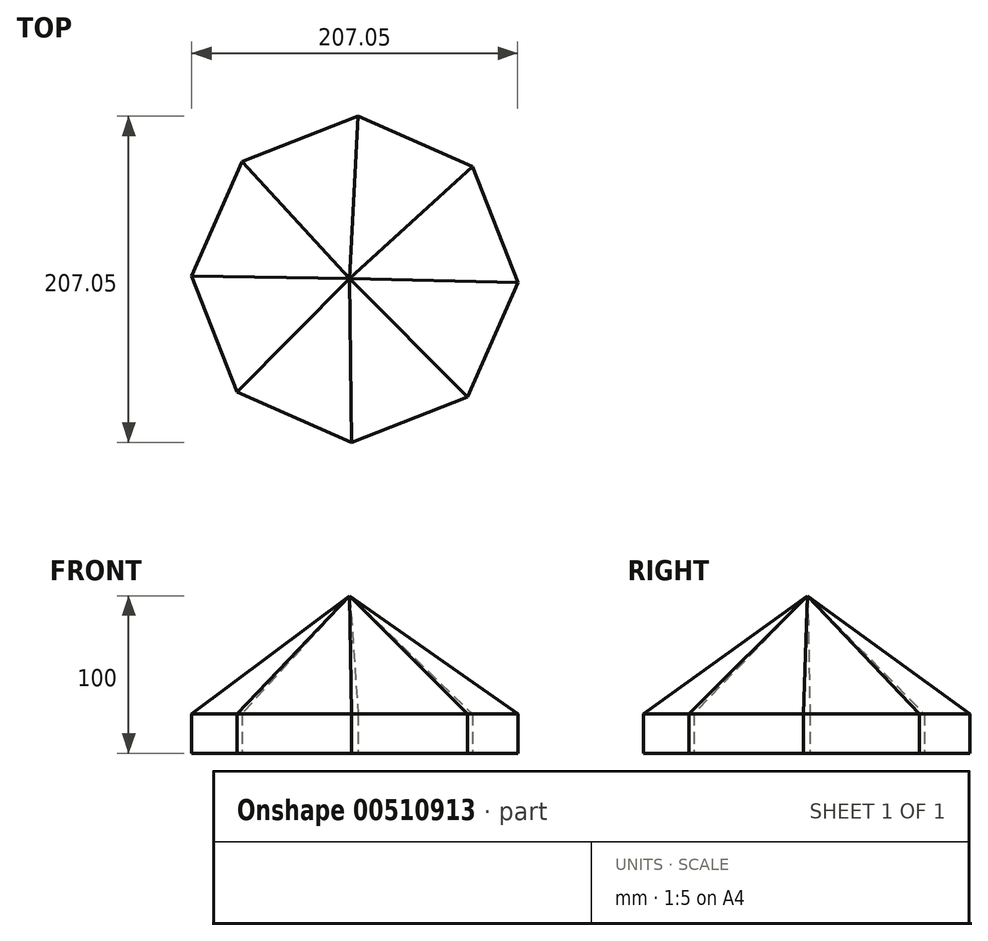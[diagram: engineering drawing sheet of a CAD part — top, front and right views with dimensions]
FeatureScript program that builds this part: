
annotation { "Feature Type Name" : "Feature", "Feature Type Description" : "" }
export const myFeature = defineFeature(function(context is Context, id is Id, definition is map)
    precondition{}
    {
        {
            var Q0;
            Q0=qCreatedBy(makeId("Top.planeOp"),FACE);
            var sketch = newSketch(context, id + "F0", { "sketchPlane" : qUnion([Q0])});
            skCircle(sketch, "E0.cCircle", {"center": v(-3.08, 12.36) * mm, "radius": 103.55 * mm, "construction": true});
            skLineSegment(sketch, "E0.0", {"start": v(-5.18, -91.16) * mm, "end": v(-77.77, -59.35) * mm});
            skLineSegment(sketch, "E0.1", {"start": v(-77.77, -59.35) * mm, "end": v(-106.6, 14.46) * mm});
            skLineSegment(sketch, "E0.2", {"start": v(-106.6, 14.46) * mm, "end": v(-74.8, 87.05) * mm});
            skLineSegment(sketch, "E0.3", {"start": v(-74.8, 87.05) * mm, "end": v(-0.98, 115.89) * mm});
            skLineSegment(sketch, "E0.4", {"start": v(-0.98, 115.89) * mm, "end": v(71.61, 84.08) * mm});
            skLineSegment(sketch, "E0.5", {"start": v(71.61, 84.08) * mm, "end": v(100.44, 10.26) * mm});
            skLineSegment(sketch, "E0.6", {"start": v(100.44, 10.26) * mm, "end": v(68.64, -62.33) * mm});
            skLineSegment(sketch, "E0.7", {"start": v(68.64, -62.33) * mm, "end": v(-5.18, -91.16) * mm});
            skSolve(sketch);
        }
        {
            var Q0;
            Q0 = qSketchRegion(id + "F0", true);
            extrude(context, id + "F1", {"entities" : qUnion([Q0]), "depth" : 25 * mm});
        }
        {
            var Q0;
            Q0=qCreatedBy(makeId("Top.planeOp"),FACE);
            cPlane(context, id + "F2", {"entities" : qUnion([Q0]), "cplaneType" : CPlaneType.OFFSET, "offset" : 100 * mm, "width" : 150 * mm, "height" : 150 * mm});
        }
        {
            var Q0;
            Q0=qCreatedBy(id+"F2.planeOp",FACE);
            var sketch = newSketch(context, id + "F3", { "sketchPlane" : qUnion([Q0])});
            skPoint(sketch, "E1", {"position": v(-6.25, 12.95) * mm});
            skSolve(sketch);
        }
        {
            var Q1;
            Q1=sQuery(id+"F3.wireOp",VERTEX,"E1");
            var Q2;
            Q2=makeQuery(id+"F1.opExtrude","CAP_FACE",FACE,{"disambiguationData":[OSD([sQuery(id+"F0.wireOp",EDGE,"E0.0"),sQuery(id+"F0.wireOp",EDGE,"E0.1"),sQuery(id+"F0.wireOp",EDGE,"E0.2"),sQuery(id+"F0.wireOp",EDGE,"E0.3"),sQuery(id+"F0.wireOp",EDGE,"E0.4"),sQuery(id+"F0.wireOp",EDGE,"E0.5"),sQuery(id+"F0.wireOp",EDGE,"E0.6"),sQuery(id+"F0.wireOp",EDGE,"E0.7")])],"isStart":false});
            loft(context, id + "F4", {"operationType" : NewBodyOperationType.ADD, "sheetProfilesArray" : [{ "sheetProfileEntities" : qUnion([Q1]) }, { "sheetProfileEntities" : qUnion([Q2]) }]});
        }
    });
